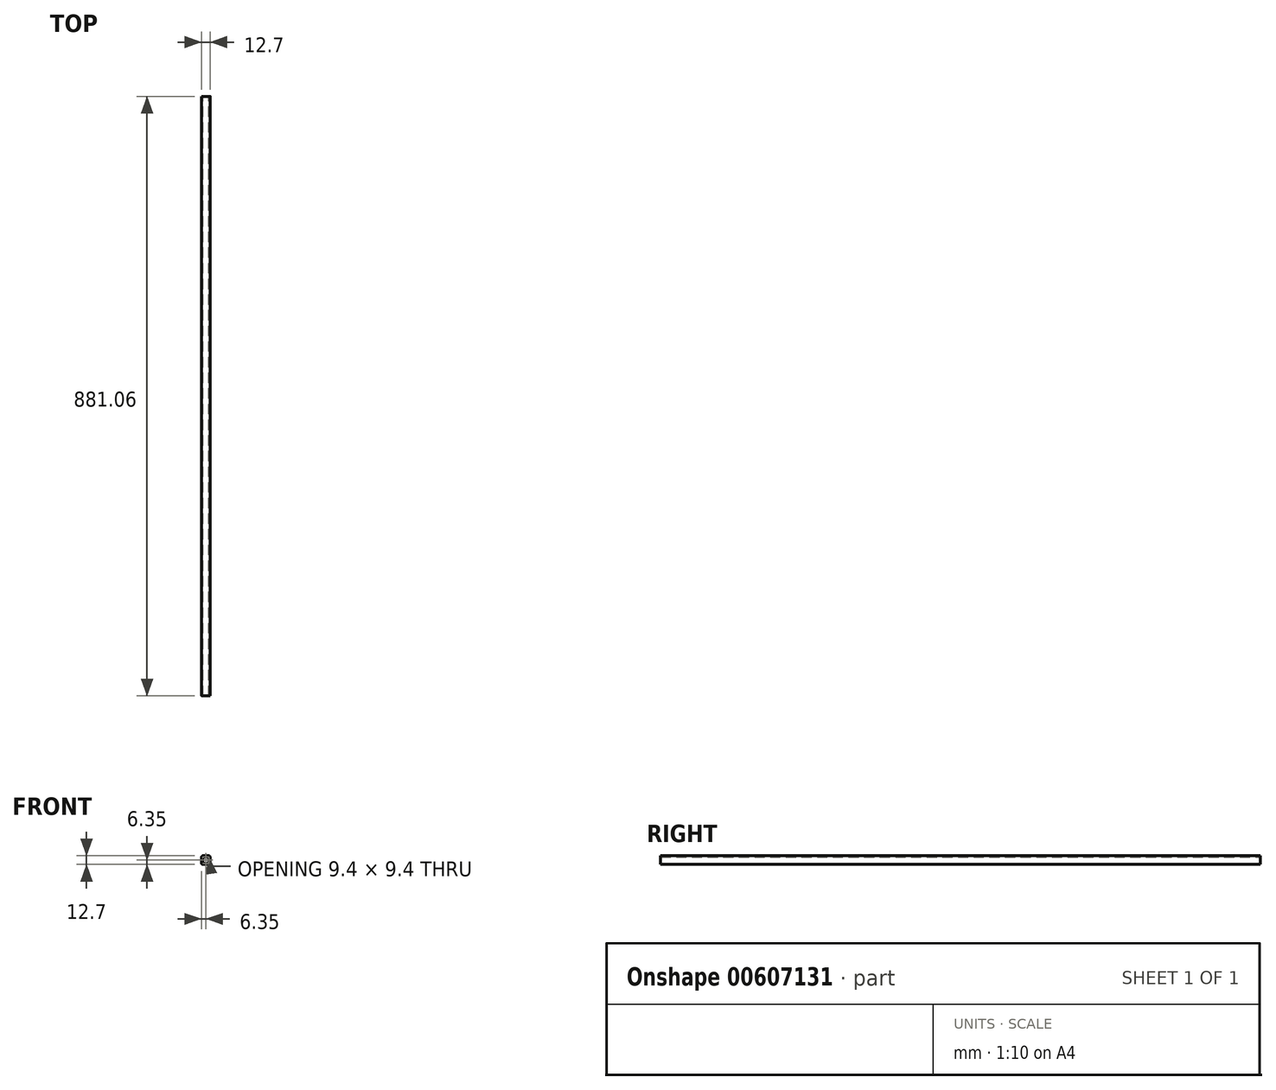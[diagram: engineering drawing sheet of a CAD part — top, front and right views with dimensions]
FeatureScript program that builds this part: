
annotation { "Feature Type Name" : "Feature", "Feature Type Description" : "" }
export const myFeature = defineFeature(function(context is Context, id is Id, definition is map)
    precondition{}
    {
        {
            var Q0;
            Q0=qCreatedBy(makeId("Front.planeOp"),FACE);
            var sketch = newSketch(context, id + "F0", { "sketchPlane" : qUnion([Q0])});
            skLineSegment(sketch, "E0.bottom", {"start": v(4.45, -6.35) * mm, "end": v(-4.45, -6.35) * mm});
            skLineSegment(sketch, "E0.top", {"start": v(4.44, 6.35) * mm, "end": v(-4.45, 6.35) * mm});
            skLineSegment(sketch, "E0.left", {"start": v(6.35, -4.45) * mm, "end": v(6.35, 4.45) * mm});
            skLineSegment(sketch, "E0.right", {"start": v(-6.35, -4.45) * mm, "end": v(-6.35, 4.45) * mm});
            skPoint(sketch, "E0.middle", {"position": v(0, 0) * mm});
            skPoint(sketch, "E1.visualSharp", {"position": v(-6.35, 6.35) * mm});
            skArc(sketch, "E1.filletArc", {"start": v(-4.45, 6.35) * mm, "mid": v(-5.8, 5.8) * mm, "end": v(-6.35, 4.45) * mm});
            skPoint(sketch, "E2.visualSharp", {"position": v(6.35, 6.35) * mm});
            skArc(sketch, "E2.filletArc", {"start": v(6.35, 4.45) * mm, "mid": v(5.8, 5.8) * mm, "end": v(4.44, 6.35) * mm});
            skPoint(sketch, "E3.visualSharp", {"position": v(6.35, -6.35) * mm});
            skArc(sketch, "E3.filletArc", {"start": v(4.45, -6.35) * mm, "mid": v(5.8, -5.8) * mm, "end": v(6.35, -4.45) * mm});
            skPoint(sketch, "E4.visualSharp", {"position": v(-6.35, -6.35) * mm});
            skArc(sketch, "E4.filletArc", {"start": v(-6.35, -4.45) * mm, "mid": v(-5.8, -5.8) * mm, "end": v(-4.45, -6.35) * mm});
            skArc(sketch, "E5.0", {"start": v(4.7, 4.45) * mm, "mid": v(4.62, 4.62) * mm, "end": v(4.44, 4.7) * mm});
            skLineSegment(sketch, "E5.1", {"start": v(4.7, -4.45) * mm, "end": v(4.7, 4.45) * mm});
            skLineSegment(sketch, "E5.2", {"start": v(4.44, 4.7) * mm, "end": v(-4.45, 4.7) * mm});
            skArc(sketch, "E5.3", {"start": v(4.45, -4.7) * mm, "mid": v(4.62, -4.62) * mm, "end": v(4.7, -4.45) * mm});
            skArc(sketch, "E5.4", {"start": v(-4.45, 4.7) * mm, "mid": v(-4.62, 4.62) * mm, "end": v(-4.7, 4.45) * mm});
            skLineSegment(sketch, "E5.5", {"start": v(-4.7, -4.45) * mm, "end": v(-4.7, 4.45) * mm});
            skArc(sketch, "E5.6", {"start": v(-4.7, -4.45) * mm, "mid": v(-4.62, -4.62) * mm, "end": v(-4.45, -4.7) * mm});
            skLineSegment(sketch, "E5.7", {"start": v(4.45, -4.7) * mm, "end": v(-4.45, -4.7) * mm});
            skArc(sketch, "E6.0", {"start": v(12.7, 4.45) * mm, "mid": v(10.28, 10.28) * mm, "end": v(4.44, 12.7) * mm});
            skSolve(sketch);
        }
        {
            var Q0;
            Q0=makeQuery(id+"F0.imprint","IMPRINT",FACE,{"disambiguationData":[TD([[makeQuery(id+"F0.imprint","IMPRINT",EDGE,{"derivedFrom":sQuery(id+"F0.wireOp",EDGE,"E0.bottom")}),-1.0]])]});
            extrude(context, id + "F1", {"entities" : qUnion([Q0]), "depth" : 881.06 * mm, "offsetDistance" : 25.4 * mm});
        }
    });
